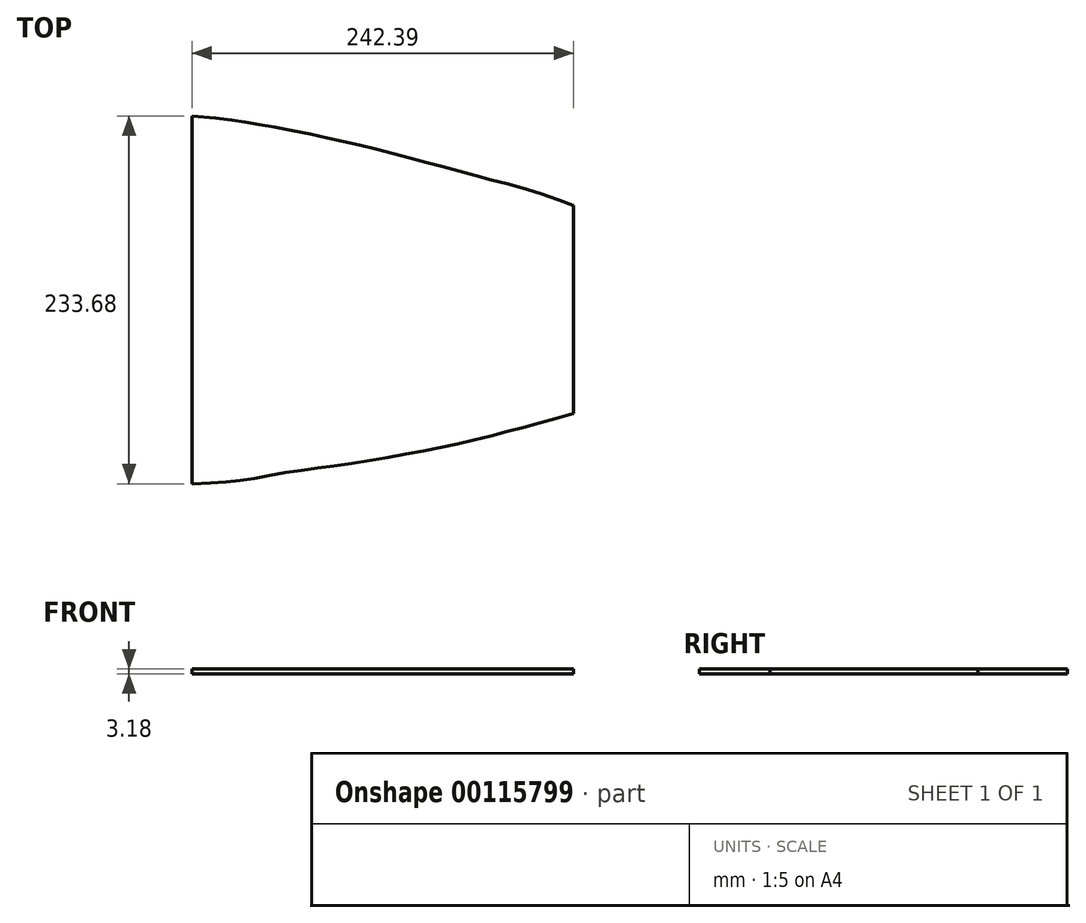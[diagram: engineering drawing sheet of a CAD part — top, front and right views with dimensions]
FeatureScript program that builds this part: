
annotation { "Feature Type Name" : "Feature", "Feature Type Description" : "" }
export const myFeature = defineFeature(function(context is Context, id is Id, definition is map)
    precondition{}
    {
        {
            var Q0;
            Q0=qCreatedBy(makeId("Top.planeOp"),FACE);
            var sketch = newSketch(context, id + "F0", { "sketchPlane" : qUnion([Q0])});
            skLineSegment(sketch, "E0", {"start": v(750.69, 62.96) * mm, "end": v(750.69, -69.12) * mm});
            skFitSpline(sketch, "E1", {"points": [v(508.3, -113.95) * mm, v(539.78, -111.73) * mm, v(568.87, -106.63) * mm, v(602.55, -101.95) * mm, v(643.34, -95.15) * mm, v(680.35, -87.7) * mm, v(714.9, -79.03) * mm, v(750.69, -69.12) * mm], "startDerivative": vector(308.01, 14.5) * mm, "endDerivative": vector(271.49, 75.26) * mm});
            skFitSpline(sketch, "E2", {"points": [v(508.3, 119.73) * mm, v(539.78, 116.2) * mm, v(560.6, 112.72) * mm, v(591.11, 106.52) * mm, v(616.16, 100.82) * mm, v(644.44, 93.63) * mm, v(670.73, 86.68) * mm, v(697.27, 79.49) * mm, v(721.24, 73.05) * mm, v(750.69, 62.96) * mm], "startDerivative": vector(425.84, -30.56) * mm, "endDerivative": vector(168.7, -69.02) * mm});
            skLineSegment(sketch, "E3", {"start": v(508.3, 119.73) * mm, "end": v(508.3, -113.95) * mm});
            skSolve(sketch);
        }
        {
            var Q0;
            Q0=makeQuery(id+"F0.imprint","IMPRINT",FACE,{"disambiguationData":[TD([[makeQuery(id+"F0.imprint","IMPRINT",EDGE,{"derivedFrom":sQuery(id+"F0.wireOp",EDGE,"E0")}),-1.0]])]});
            extrude(context, id + "F1", {"entities" : qUnion([Q0]), "depth" : 3.17 * mm});
        }
    });
